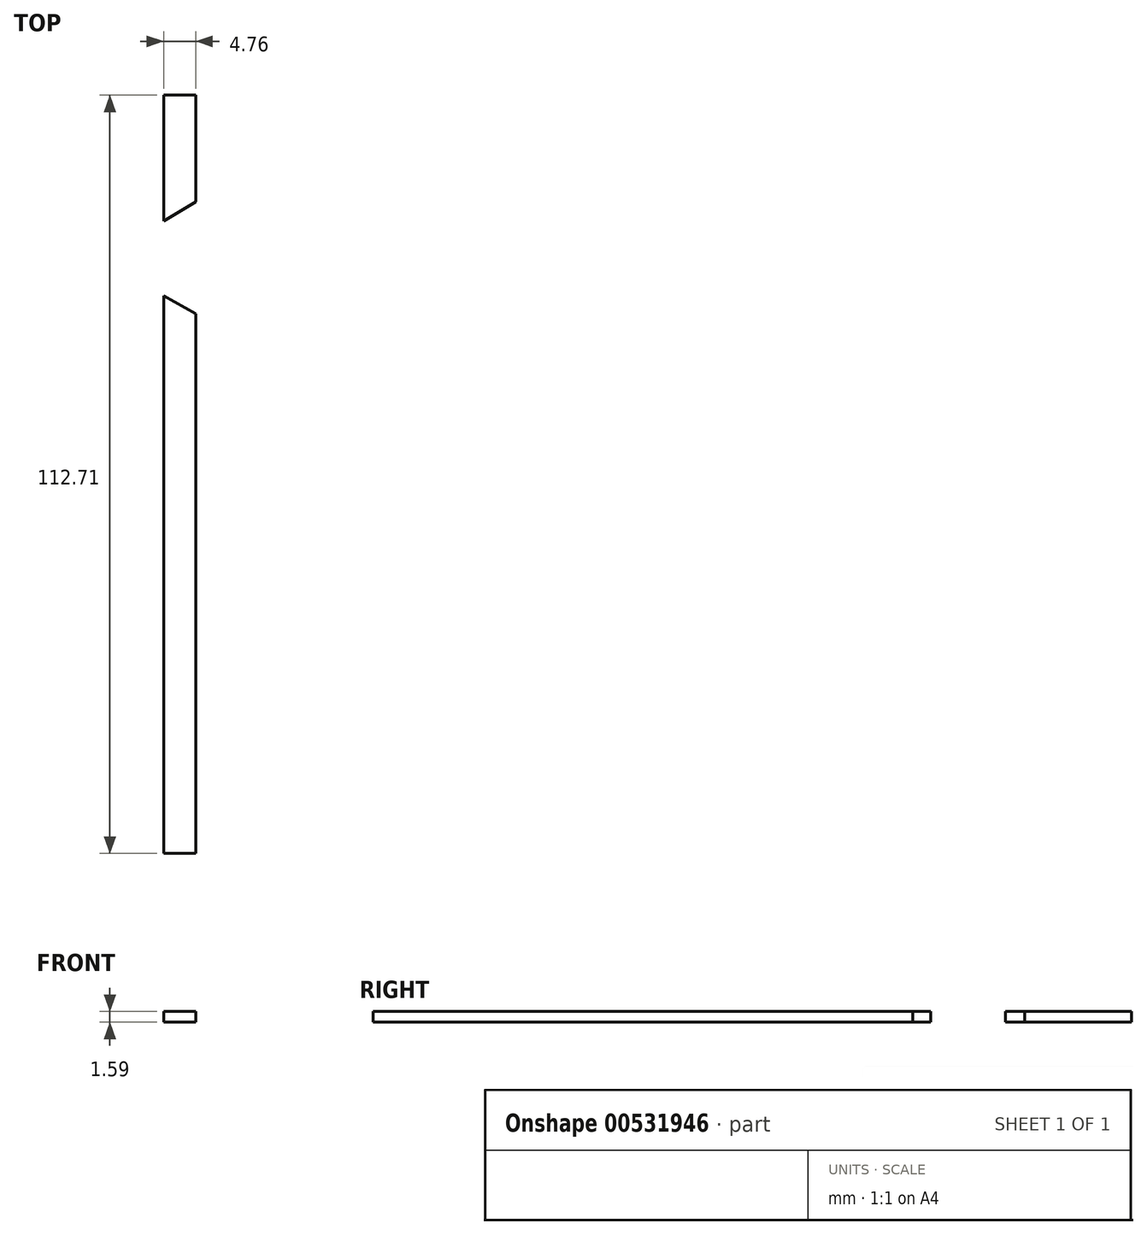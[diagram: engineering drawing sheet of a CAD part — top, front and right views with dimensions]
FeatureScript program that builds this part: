
annotation { "Feature Type Name" : "Feature", "Feature Type Description" : "" }
export const myFeature = defineFeature(function(context is Context, id is Id, definition is map)
    precondition{}
    {
        {
            var Q0;
            Q0=qCreatedBy(makeId("Top.planeOp"),FACE);
            var sketch = newSketch(context, id + "F0", { "sketchPlane" : qUnion([Q0])});
            skLineSegment(sketch, "E0.bottom", {"start": v(-4.76, 80.33) * mm, "end": v(0, 80.33) * mm});
            skLineSegment(sketch, "E0.top", {"start": v(-4.76, -32.38) * mm, "end": v(0, -32.38) * mm});
            skLineSegment(sketch, "E0.left", {"start": v(-4.76, 80.33) * mm, "end": v(-4.76, -32.38) * mm});
            skLineSegment(sketch, "E0.right", {"start": v(0, 80.33) * mm, "end": v(0, -32.38) * mm});
            skLineSegment(sketch, "E1", {"start": v(0, 64.46) * mm, "end": v(-4.76, 61.6) * mm});
            skLineSegment(sketch, "E2", {"start": v(0.1, 47.79) * mm, "end": v(-4.76, 50.48) * mm});
            skSolve(sketch);
        }
        {
            var Q0;
            {var subQ0=sQuery(id+"F0.wireOp",EDGE,"E0.bottom");Q0=makeQuery(id+"F0.imprint","IMPRINT",FACE,{"disambiguationData":[TD([[makeQuery(id+"F0.imprint","IMPRINT",EDGE,{"derivedFrom":subQ0}),-1.0]])]});}
            var Q1;
            {var subQ0=sQuery(id+"F0.wireOp",EDGE,"E0.top");Q1=makeQuery(id+"F0.imprint","IMPRINT",FACE,{"disambiguationData":[TD([[makeQuery(id+"F0.imprint","IMPRINT",EDGE,{"derivedFrom":subQ0}),1.0]])]});}
            extrude(context, id + "F1", {"entities" : qUnion([Q0, Q1]), "depth" : 1.59 * mm, "offsetDistance" : 25.4 * mm});
        }
    });
